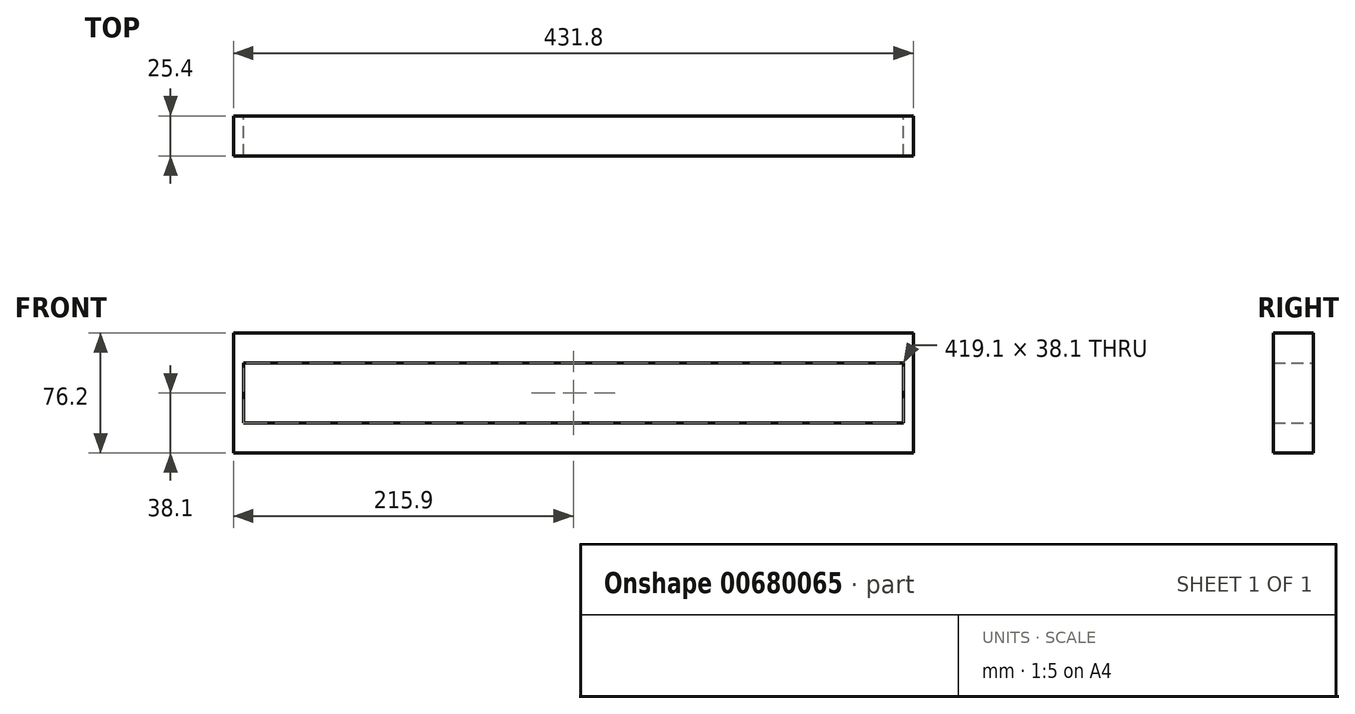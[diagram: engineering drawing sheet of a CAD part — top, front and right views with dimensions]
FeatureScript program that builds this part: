
annotation { "Feature Type Name" : "Feature", "Feature Type Description" : "" }
export const myFeature = defineFeature(function(context is Context, id is Id, definition is map)
    precondition{}
    {
        {
            var Q0;
            Q0=qCreatedBy(makeId("Front.planeOp"),FACE);
            var sketch = newSketch(context, id + "F0", { "sketchPlane" : qUnion([Q0])});
            skLineSegment(sketch, "E0.bottom", {"start": v(-215.9, 38.1) * mm, "end": v(215.9, 38.1) * mm});
            skLineSegment(sketch, "E0.left", {"start": v(-215.9, 38.1) * mm, "end": v(-215.9, -38.1) * mm});
            skLineSegment(sketch, "E0.right", {"start": v(215.9, 38.1) * mm, "end": v(215.9, -38.1) * mm});
            skPoint(sketch, "E0.middle", {"position": v(0, 0) * mm});
            skLineSegment(sketch, "E1.top", {"start": v(-215.9, -38.1) * mm, "end": v(215.9, -38.1) * mm});
            skLineSegment(sketch, "E1.left", {"start": v(-215.9, 30.51) * mm, "end": v(-215.9, -38.1) * mm});
            skLineSegment(sketch, "E1.right", {"start": v(215.9, 30.51) * mm, "end": v(215.9, -38.1) * mm});
            skPoint(sketch, "E1.middle", {"position": v(0, -3.8) * mm});
            skLineSegment(sketch, "E2.left", {"start": v(-215.9, 30.51) * mm, "end": v(-215.9, -32.99) * mm});
            skLineSegment(sketch, "E3.left", {"start": v(215.9, 30.51) * mm, "end": v(215.9, -32.99) * mm});
            skLineSegment(sketch, "E4.bottom", {"start": v(-209.55, -19.05) * mm, "end": v(209.55, -19.05) * mm});
            skLineSegment(sketch, "E4.top", {"start": v(-209.55, 19.05) * mm, "end": v(209.55, 19.05) * mm});
            skLineSegment(sketch, "E4.left", {"start": v(-209.55, -19.05) * mm, "end": v(-209.55, 19.05) * mm});
            skLineSegment(sketch, "E4.right", {"start": v(209.55, -19.05) * mm, "end": v(209.55, 19.05) * mm});
            skSolve(sketch);
        }
        {
            var Q0;
            {var subQ0=sQuery(id+"F0.wireOp",EDGE,"E1.bottom");Q0=makeQuery(id+"F0.imprint","IMPRINT",FACE,{"disambiguationData":[TD([[makeQuery(id+"F0.imprint","IMPRINT",EDGE,{"derivedFrom":subQ0}),-1.0]])]});}
            var Q1;
            {var subQ5=sQuery(id+"F0.wireOp",EDGE,"E2.bottom");Q1=makeQuery(id+"F0.imprint","IMPRINT",FACE,{"disambiguationData":[TD([[makeQuery(id+"F0.imprint","IMPRINT",EDGE,{"derivedFrom":subQ5}),-1.0]])]});}
            var Q2;
            {var subQ5=sQuery(id+"F0.wireOp",EDGE,"E3.bottom");Q2=makeQuery(id+"F0.imprint","IMPRINT",FACE,{"disambiguationData":[TD([[makeQuery(id+"F0.imprint","IMPRINT",EDGE,{"derivedFrom":subQ5}),1.0]])]});}
            var Q3;
            {var subQ0=sQuery(id+"F0.wireOp",EDGE,"E0.right");Q3=makeQuery(id+"F0.imprint","IMPRINT",FACE,{"disambiguationData":[TD([[makeQuery(id+"F0.imprint","IMPRINT",EDGE,{"derivedFrom":subQ0}),-1.0]])]});}
            var Q4;
            {var subQ5=sQuery(id+"F0.wireOp",EDGE,"E0.top");Q4=makeQuery(id+"F0.imprint","IMPRINT",FACE,{"disambiguationData":[TD([[makeQuery(id+"F0.imprint","IMPRINT",EDGE,{"derivedFrom":subQ5}),1.0]])]});}
            var Q5;
            {var subQ0=sQuery(id+"F0.wireOp",EDGE,"E0.left");Q5=makeQuery(id+"F0.imprint","IMPRINT",FACE,{"disambiguationData":[TD([[makeQuery(id+"F0.imprint","IMPRINT",EDGE,{"derivedFrom":subQ0}),1.0]])]});}
            var Q6;
            {var subQ1=sQuery(id+"F0.wireOp",EDGE,"E0.left");Q6=makeQuery(id+"F0.imprint","IMPRINT",FACE,{"disambiguationData":[TD([[makeQuery(id+"F0.imprint","IMPRINT",EDGE,{"derivedFrom":subQ1}),-1.0]])]});}
            var Q7;
            {var subQ1=sQuery(id+"F0.wireOp",EDGE,"E0.right");Q7=makeQuery(id+"F0.imprint","IMPRINT",FACE,{"disambiguationData":[TD([[makeQuery(id+"F0.imprint","IMPRINT",EDGE,{"derivedFrom":subQ1}),1.0]])]});}
            extrude(context, id + "F1", {"entities" : qUnion([Q0, Q1, Q2, Q3, Q4, Q5, Q6, Q7]), "depth" : 12.7 * mm, "offsetDistance" : 25.4 * mm});
        }
        {
            var Q0;
            Q0 = qSketchRegion(id + "F0", true);
            extrude(context, id + "F2", {"entities" : qUnion([Q0]), "operationType" : NewBodyOperationType.ADD, "depth" : 25.4 * mm, "offsetDistance" : 25.4 * mm});
        }
    });
